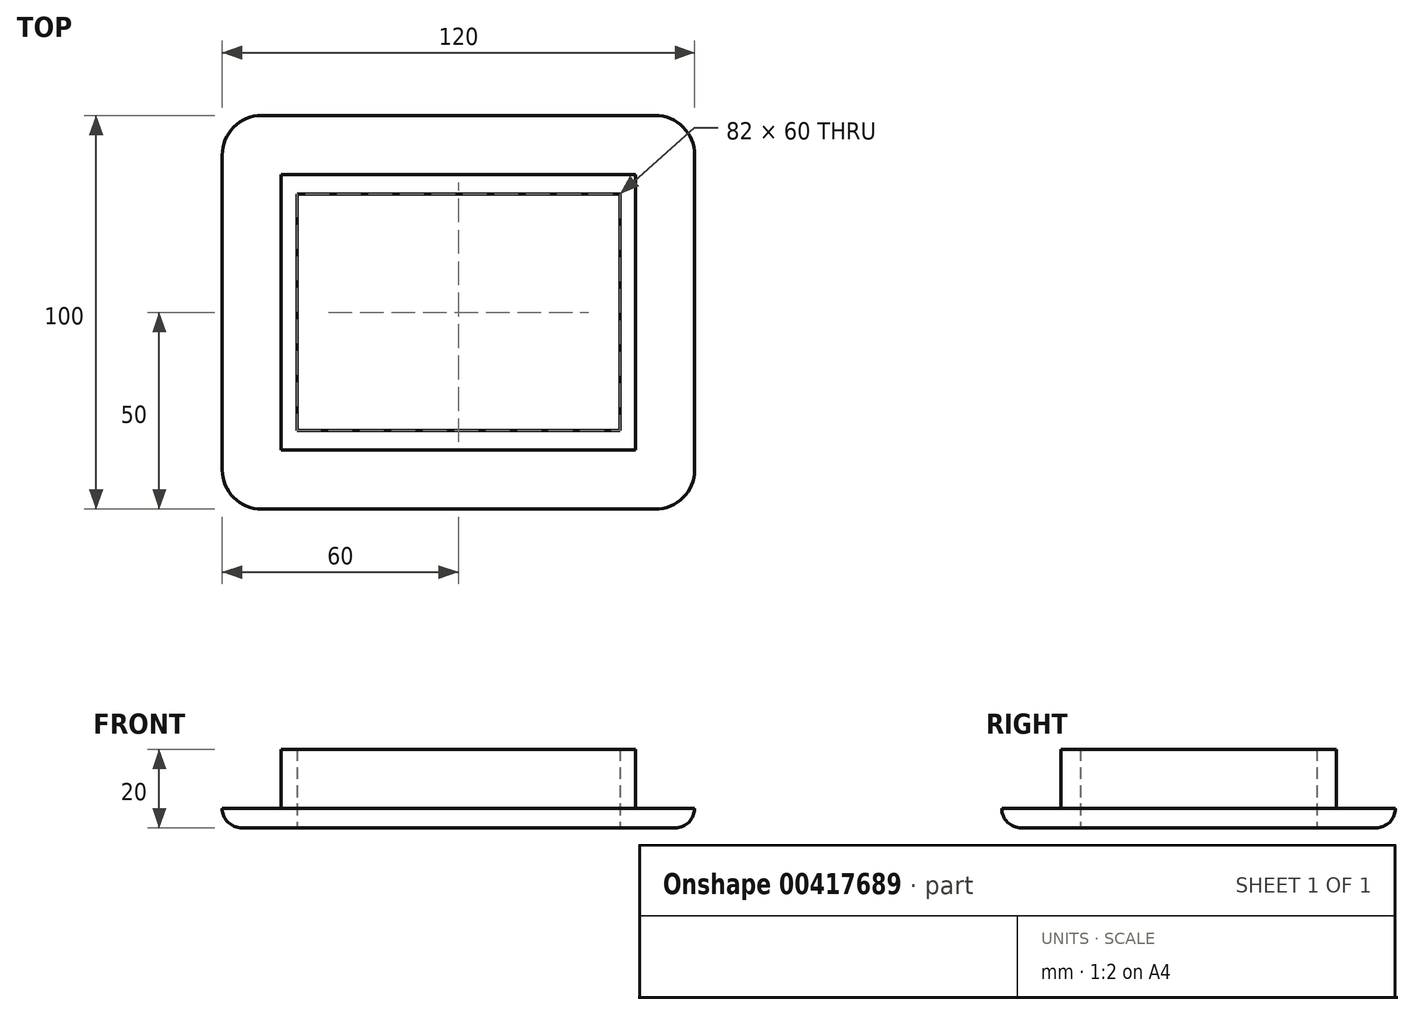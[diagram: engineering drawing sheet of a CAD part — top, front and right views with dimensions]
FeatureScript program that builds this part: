
annotation { "Feature Type Name" : "Feature", "Feature Type Description" : "" }
export const myFeature = defineFeature(function(context is Context, id is Id, definition is map)
    precondition{}
    {
        {
            var Q0;
            Q0=qCreatedBy(makeId("Top.planeOp"),FACE);
            var sketch = newSketch(context, id + "F0", { "sketchPlane" : qUnion([Q0])});
            skLineSegment(sketch, "E0.bottom", {"start": v(45, -35) * mm, "end": v(-45, -35) * mm});
            skLineSegment(sketch, "E0.top", {"start": v(45, 35) * mm, "end": v(-45, 35) * mm});
            skLineSegment(sketch, "E0.left", {"start": v(45, -35) * mm, "end": v(45, 35) * mm});
            skLineSegment(sketch, "E0.right", {"start": v(-45, -35) * mm, "end": v(-45, 35) * mm});
            skPoint(sketch, "E0.middle", {"position": v(0, 0) * mm});
            skLineSegment(sketch, "E1.bottom", {"start": v(41, -30) * mm, "end": v(-41, -30) * mm});
            skLineSegment(sketch, "E1.top", {"start": v(41, 30) * mm, "end": v(-41, 30) * mm});
            skLineSegment(sketch, "E1.left", {"start": v(41, -30) * mm, "end": v(41, 30) * mm});
            skLineSegment(sketch, "E1.right", {"start": v(-41, -30) * mm, "end": v(-41, 30) * mm});
            skLineSegment(sketch, "E2.bottom", {"start": v(50, -50) * mm, "end": v(-50, -50) * mm});
            skLineSegment(sketch, "E2.top", {"start": v(50, 50) * mm, "end": v(-50, 50) * mm});
            skLineSegment(sketch, "E2.left", {"start": v(60, -40) * mm, "end": v(60, 40) * mm});
            skLineSegment(sketch, "E2.right", {"start": v(-60, -40) * mm, "end": v(-60, 40) * mm});
            skPoint(sketch, "E3.visualSharp", {"position": v(-60, 50) * mm});
            skArc(sketch, "E3.filletArc", {"start": v(-50, 50) * mm, "mid": v(-57.07, 47.07) * mm, "end": v(-60, 40) * mm});
            skPoint(sketch, "E4.visualSharp", {"position": v(60, 50) * mm});
            skArc(sketch, "E4.filletArc", {"start": v(60, 40) * mm, "mid": v(57.07, 47.07) * mm, "end": v(50, 50) * mm});
            skPoint(sketch, "E5.visualSharp", {"position": v(60, -50) * mm});
            skArc(sketch, "E5.filletArc", {"start": v(50, -50) * mm, "mid": v(57.07, -47.07) * mm, "end": v(60, -40) * mm});
            skPoint(sketch, "E6.visualSharp", {"position": v(-60, -50) * mm});
            skArc(sketch, "E6.filletArc", {"start": v(-60, -40) * mm, "mid": v(-57.07, -47.07) * mm, "end": v(-50, -50) * mm});
            skSolve(sketch);
        }
        {
            var Q0;
            Q0=makeQuery(id+"F0.imprint","IMPRINT",FACE,{"disambiguationData":[TD([[makeQuery(id+"F0.imprint","IMPRINT",EDGE,{"derivedFrom":sQuery(id+"F0.wireOp",EDGE,"E0.bottom")}),1.0]])]});
            var Q1;
            Q1=makeQuery(id+"F0.imprint","IMPRINT",FACE,{"disambiguationData":[TD([[makeQuery(id+"F0.imprint","IMPRINT",EDGE,{"derivedFrom":sQuery(id+"F0.wireOp",EDGE,"LUdHdZwW-3mhZ-CL01-7axV-JborbAGbrk8q.bottom")}),-1.0]])]});
            var Q2;
            Q2=makeQuery(id+"F0.imprint","IMPRINT",FACE,{"disambiguationData":[TD([[makeQuery(id+"F0.imprint","IMPRINT",EDGE,{"derivedFrom":sQuery(id+"F0.wireOp",EDGE,"3ThagGFS-sa57-GH8z-zDcM-49cpQbPTO54m.bottom")}),-1.0]])]});
            var Q3;
            Q3=makeQuery(id+"F0.imprint","IMPRINT",FACE,{"disambiguationData":[TD([[makeQuery(id+"F0.imprint","IMPRINT",EDGE,{"derivedFrom":sQuery(id+"F0.wireOp",EDGE,"E0.bottom")}),-1.0]])]});
            extrude(context, id + "F1", {"entities" : qUnion([Q0, Q1, Q2, Q3]), "depth" : 5 * mm});
        }
        {
            var Q0;
            Q0=makeQuery(id+"F0.imprint","IMPRINT",FACE,{"disambiguationData":[TD([[makeQuery(id+"F0.imprint","IMPRINT",EDGE,{"derivedFrom":sQuery(id+"F0.wireOp",EDGE,"E0.bottom")}),-1.0]])]});
            var Q1;
            Q1=makeQuery(id+"F0.imprint","IMPRINT",FACE,{"disambiguationData":[TD([[makeQuery(id+"F0.imprint","IMPRINT",EDGE,{"derivedFrom":sQuery(id+"F0.wireOp",EDGE,"E1.bottom")}),-1.0]])]});
            extrude(context, id + "F2", {"entities" : qUnion([Q0, Q1]), "operationType" : NewBodyOperationType.ADD, "depth" : 20 * mm});
        }
        {
            var Q0;
            Q0=makeQuery(id+"F0.imprint","IMPRINT",FACE,{"disambiguationData":[TD([[makeQuery(id+"F0.imprint","IMPRINT",EDGE,{"derivedFrom":sQuery(id+"F0.wireOp",EDGE,"E1.bottom")}),-1.0]])]});
            extrude(context, id + "F3", {"entities" : qUnion([Q0]), "operationType" : NewBodyOperationType.REMOVE, "depth" : 20 * mm});
        }
        {
            var Q0;
            Q0=makeQuery(id+"F1.opExtrude","CAP_EDGE",EDGE,{"disambiguationData":[OSD([sQuery(id+"F0.wireOp",EDGE,"E5.filletArc")])],"isStart":true});
            fillet(context, id + "F4", {"entities" : qUnion([Q0]), "radius" : 5 * mm, "tangentPropagation" : true, "allowEdgeOverflow" : false});
        }
    });
